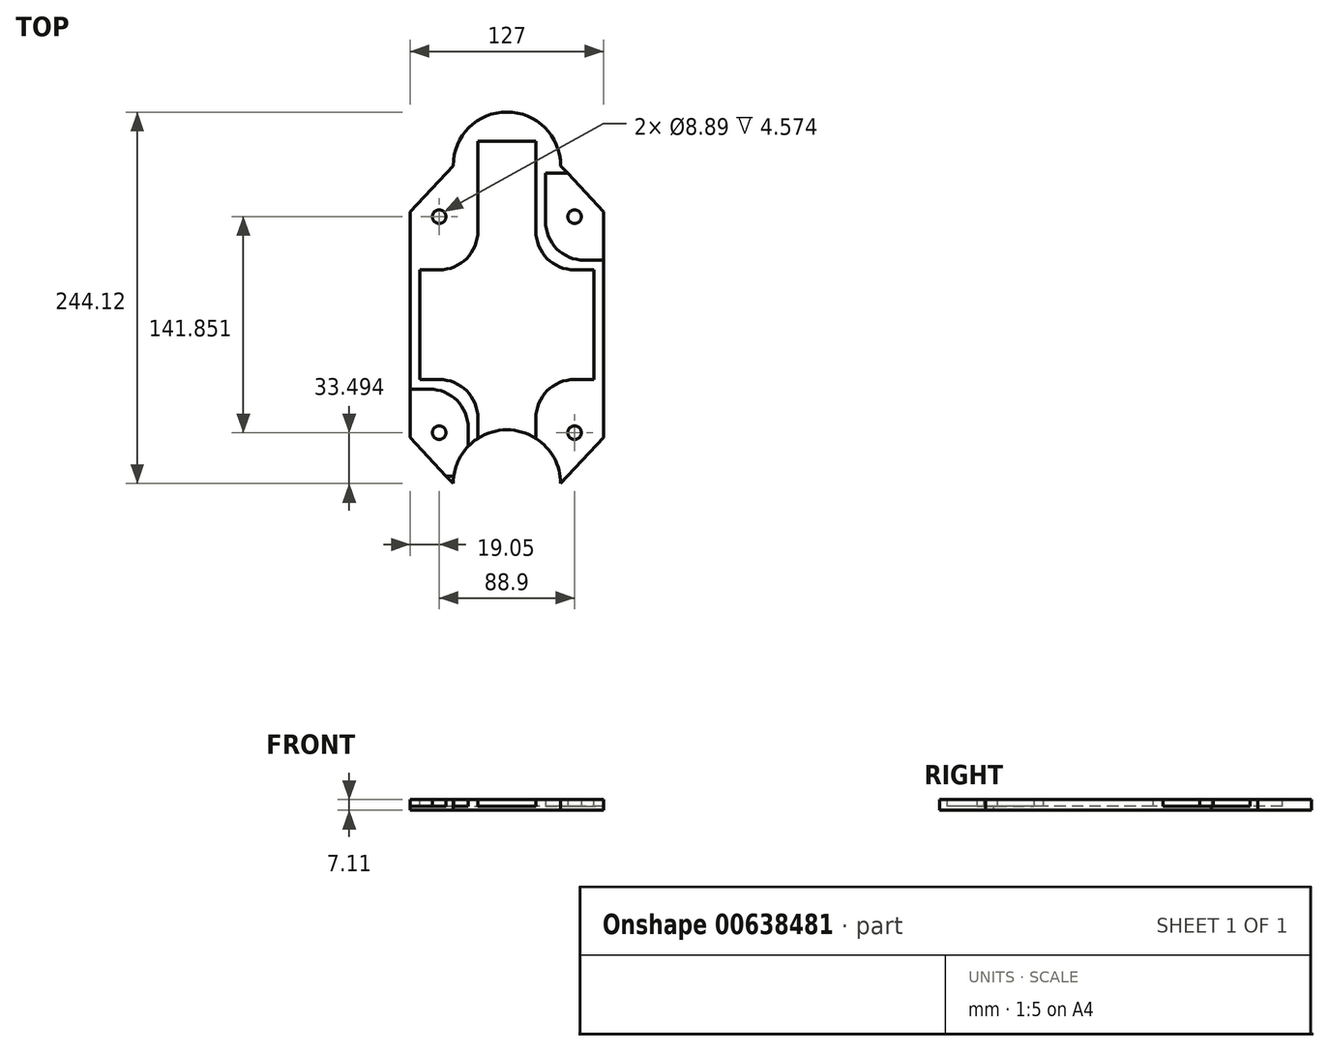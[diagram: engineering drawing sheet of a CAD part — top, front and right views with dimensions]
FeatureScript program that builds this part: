
annotation { "Feature Type Name" : "Feature", "Feature Type Description" : "" }
export const myFeature = defineFeature(function(context is Context, id is Id, definition is map)
    precondition{}
    {
        {
            var Q0;
            Q0=qCreatedBy(makeId("Top.planeOp"),FACE);
            var sketch = newSketch(context, id + "F0", { "sketchPlane" : qUnion([Q0])});
            skCircle(sketch, "E0", {"center": v(0, 104.42) * mm, "radius": 35.28 * mm});
            skLineSegment(sketch, "E1.bottom", {"start": v(63.5, 74.1) * mm, "end": v(18.06, 74.1) * mm});
            skLineSegment(sketch, "E1.left", {"start": v(63.5, 74.1) * mm, "end": v(63.5, 0) * mm});
            skLineSegment(sketch, "E1.right", {"start": v(-63.5, 74.1) * mm, "end": v(-63.5, 0) * mm});
            skPoint(sketch, "E1.middle", {"position": v(0, 0) * mm});
            skLineSegment(sketch, "E2", {"start": v(35.28, 104.42) * mm, "end": v(63.5, 74.1) * mm});
            skLineSegment(sketch, "E3", {"start": v(-35.28, 104.42) * mm, "end": v(-63.5, 74.1) * mm});
            skLineSegment(sketch, "E4", {"start": v(-63.5, 0) * mm, "end": v(63.5, 0) * mm});
            skCircle(sketch, "E5.MirrorC", {"center": v(0, -104.42) * mm, "radius": 35.28 * mm});
            skLineSegment(sketch, "E6.MirrorCS", {"start": v(63.5, -74.1) * mm, "end": v(18.06, -74.1) * mm});
            skLineSegment(sketch, "E7.MirrorCS", {"start": v(63.5, -74.1) * mm, "end": v(63.5, 0) * mm});
            skLineSegment(sketch, "E8.MirrorCS", {"start": v(-63.5, -74.1) * mm, "end": v(-63.5, 0) * mm});
            skLineSegment(sketch, "E9.MirrorCS", {"start": v(35.28, -104.42) * mm, "end": v(63.5, -74.1) * mm});
            skLineSegment(sketch, "E10.MirrorCS", {"start": v(-35.28, -104.42) * mm, "end": v(-63.5, -74.1) * mm});
            skLineSegment(sketch, "E11.trimOffspring", {"start": v(-18.06, 74.1) * mm, "end": v(-63.5, 74.1) * mm});
            skLineSegment(sketch, "E12.trimOffspring", {"start": v(-18.06, -74.1) * mm, "end": v(-63.5, -74.1) * mm});
            skSolve(sketch);
        }
        {
            var Q0;
            {var subQ0=sQuery(id+"F0.wireOp",EDGE,"E1.bottom");Q0=makeQuery(id+"F0.imprint","IMPRINT",FACE,{"disambiguationData":[TD([[makeQuery(id+"F0.imprint","IMPRINT",EDGE,{"derivedFrom":subQ0}),1.0]])]});}
            var Q1;
            Q1=makeQuery(id+"F0.imprint","IMPRINT",FACE,{"disambiguationData":[TD([[makeQuery(id+"F0.imprint","IMPRINT",EDGE,{"derivedFrom":sQuery(id+"F0.wireOp",EDGE,"E4")}),-1.0]])]});
            var Q2;
            {var subQ0=sQuery(id+"F0.wireOp",EDGE,"E5.MirrorC");var subQ1=makeQuery(id+"F0.imprint","INTERSECT",VERTEX,{"derivedFrom":[subQ0,sQuery(id+"F0.wireOp",EDGE,"E9.MirrorCS")]});Q2=makeQuery(id+"F0.imprint","IMPRINT",FACE,{"disambiguationData":[TD([[makeQuery(id+"F0.imprint","IMPRINT",EDGE,{"disambiguationData":[TD([[subQ1,-1.0]])],"derivedFrom":subQ0}),-1.0]])]});}
            var Q3;
            {var subQ0=sQuery(id+"F0.wireOp",EDGE,"E10.MirrorCS");Q3=makeQuery(id+"F0.imprint","IMPRINT",FACE,{"disambiguationData":[TD([[makeQuery(id+"F0.imprint","IMPRINT",EDGE,{"derivedFrom":subQ0}),-1.0]])]});}
            var Q4;
            {var subQ0=sQuery(id+"F0.wireOp",EDGE,"E6.MirrorCS");Q4=makeQuery(id+"F0.imprint","IMPRINT",FACE,{"disambiguationData":[TD([[makeQuery(id+"F0.imprint","IMPRINT",EDGE,{"derivedFrom":subQ0}),1.0]])]});}
            var Q5;
            {var subQ0=sQuery(id+"F0.wireOp",EDGE,"E0");var subQ1=makeQuery(id+"F0.imprint","INTERSECT",VERTEX,{"derivedFrom":[subQ0,sQuery(id+"F0.wireOp",EDGE,"E2")]});Q5=makeQuery(id+"F0.imprint","IMPRINT",FACE,{"disambiguationData":[TD([[makeQuery(id+"F0.imprint","IMPRINT",EDGE,{"disambiguationData":[TD([[subQ1,-1.0]])],"derivedFrom":subQ0}),1.0]])]});}
            var Q6;
            {var subQ0=sQuery(id+"F0.wireOp",EDGE,"E1.bottom");Q6=makeQuery(id+"F0.imprint","IMPRINT",FACE,{"disambiguationData":[TD([[makeQuery(id+"F0.imprint","IMPRINT",EDGE,{"derivedFrom":subQ0}),-1.0]])]});}
            var Q7;
            {var subQ0=sQuery(id+"F0.wireOp",EDGE,"E3");Q7=makeQuery(id+"F0.imprint","IMPRINT",FACE,{"disambiguationData":[TD([[makeQuery(id+"F0.imprint","IMPRINT",EDGE,{"derivedFrom":subQ0}),1.0]])]});}
            extrude(context, id + "F1", {"entities" : qUnion([Q0, Q1, Q2, Q3, Q4, Q5, Q6, Q7]), "depth" : 50.8 * mm, "offsetDistance" : 25.4 * mm});
        }
        {
            var Q0;
            Q0=makeQuery(id+"F1.opExtrude","SWEPT_FACE",FACE,{"disambiguationData":[OSD([sQuery(id+"F0.wireOp",EDGE,"E1.left"),sQuery(id+"F0.wireOp",EDGE,"E7.MirrorCS")])]});
            var sketch = newSketch(context, id + "F2", { "sketchPlane" : qUnion([Q0])});
            skLineSegment(sketch, "E13.0.0", {"start": v(-74.1, 0) * mm, "end": v(74.1, 0) * mm});
            skLineSegment(sketch, "E13.0.1", {"start": v(74.1, 0) * mm, "end": v(74.1, 50.8) * mm});
            skLineSegment(sketch, "E13.0.2", {"start": v(74.1, 50.8) * mm, "end": v(-74.1, 50.8) * mm});
            skLineSegment(sketch, "E13.0.3", {"start": v(-74.1, 50.8) * mm, "end": v(-74.1, 0) * mm});
            skLineSegment(sketch, "E14.0.0", {"start": v(-104.42, 0) * mm, "end": v(-74.1, 0) * mm});
            skLineSegment(sketch, "E14.0.1", {"start": v(-74.1, 0) * mm, "end": v(-74.1, 50.8) * mm});
            skLineSegment(sketch, "E14.0.2", {"start": v(-74.1, 50.8) * mm, "end": v(-104.42, 50.8) * mm});
            skLineSegment(sketch, "E14.0.3", {"start": v(-104.42, 50.8) * mm, "end": v(-104.42, 0) * mm});
            skLineSegment(sketch, "E15.bottom", {"start": v(-42.35, 43.18) * mm, "end": v(-99.5, 43.18) * mm});
            skLineSegment(sketch, "E15.top", {"start": v(-42.35, 7.62) * mm, "end": v(-99.5, 7.62) * mm});
            skLineSegment(sketch, "E15.left", {"start": v(-42.35, 43.18) * mm, "end": v(-42.35, 7.62) * mm});
            skLineSegment(sketch, "E15.right", {"start": v(-99.5, 43.18) * mm, "end": v(-99.5, 7.62) * mm});
            skLineSegment(sketch, "E16.MirrorCS", {"start": v(99.5, 43.18) * mm, "end": v(99.5, 7.62) * mm});
            skLineSegment(sketch, "E17.MirrorCS", {"start": v(42.35, 43.18) * mm, "end": v(42.35, 7.62) * mm});
            skLineSegment(sketch, "E18.MirrorCS", {"start": v(42.35, 7.62) * mm, "end": v(99.5, 7.62) * mm});
            skLineSegment(sketch, "E19.MirrorCS", {"start": v(42.35, 43.18) * mm, "end": v(99.5, 43.18) * mm});
            skSolve(sketch);
        }
        {
            var Q0;
            {var subQ5=sQuery(id+"F2.wireOp",EDGE,"E15.left");Q0=makeQuery(id+"F2.imprint","IMPRINT",FACE,{"disambiguationData":[TD([[makeQuery(id+"F2.imprint","IMPRINT",EDGE,{"derivedFrom":subQ5}),-1.0]])]});}
            var Q1;
            {var subQ5=sQuery(id+"F2.wireOp",EDGE,"E15.right");Q1=makeQuery(id+"F2.imprint","IMPRINT",FACE,{"disambiguationData":[TD([[makeQuery(id+"F2.imprint","IMPRINT",EDGE,{"derivedFrom":subQ5}),1.0]])]});}
            var Q2;
            {var subQ5=sQuery(id+"F2.wireOp",EDGE,"E16.MirrorCS");Q2=makeQuery(id+"F2.imprint","IMPRINT",FACE,{"disambiguationData":[TD([[makeQuery(id+"F2.imprint","IMPRINT",EDGE,{"derivedFrom":subQ5}),-1.0]])]});}
            var Q3;
            {var subQ5=sQuery(id+"F2.wireOp",EDGE,"E17.MirrorCS");Q3=makeQuery(id+"F2.imprint","IMPRINT",FACE,{"disambiguationData":[TD([[makeQuery(id+"F2.imprint","IMPRINT",EDGE,{"derivedFrom":subQ5}),1.0]])]});}
            extrude(context, id + "F3", {"entities" : qUnion([Q0, Q1, Q2, Q3]), "operationType" : NewBodyOperationType.REMOVE, "oppositeDirection" : true, "depth" : 38.1 * mm, "offsetDistance" : 25.4 * mm});
        }
        {
            var Q0;
            Q0=makeQuery(id+"F1.opExtrude","SWEPT_FACE",FACE,{"disambiguationData":[OSD([sQuery(id+"F0.wireOp",EDGE,"E1.right"),sQuery(id+"F0.wireOp",EDGE,"E8.MirrorCS")])]});
            var sketch = newSketch(context, id + "F4", { "sketchPlane" : qUnion([Q0])});
            skLineSegment(sketch, "E20.bottom", {"start": v(-99.5, 43.18) * mm, "end": v(-42.35, 43.18) * mm});
            skLineSegment(sketch, "E20.top", {"start": v(-99.5, 7.62) * mm, "end": v(-42.35, 7.62) * mm});
            skLineSegment(sketch, "E20.left", {"start": v(-99.5, 43.18) * mm, "end": v(-99.5, 7.62) * mm});
            skLineSegment(sketch, "E20.right", {"start": v(-42.35, 43.18) * mm, "end": v(-42.35, 7.62) * mm});
            skPoint(sketch, "E20.middle", {"position": v(-70.93, 25.4) * mm});
            skPoint(sketch, "E20.middle.positionSnap0", {"position": v(-74.1, 25.4) * mm});
            skPoint(sketch, "E20.centerSnap0", {"position": v(-74.1, 25.4) * mm});
            skPoint(sketch, "E21.MirrorP", {"position": v(74.1, 25.4) * mm});
            skLineSegment(sketch, "E22.MirrorCS", {"start": v(42.35, 43.18) * mm, "end": v(42.35, 7.62) * mm});
            skPoint(sketch, "E23.MirrorP", {"position": v(70.93, 25.4) * mm});
            skLineSegment(sketch, "E24.MirrorCS", {"start": v(99.5, 43.18) * mm, "end": v(99.5, 7.62) * mm});
            skLineSegment(sketch, "E25.MirrorCS", {"start": v(99.5, 43.18) * mm, "end": v(42.35, 43.18) * mm});
            skLineSegment(sketch, "E26.MirrorCS", {"start": v(99.5, 7.62) * mm, "end": v(42.35, 7.62) * mm});
            skSolve(sketch);
        }
        {
            var Q0;
            {var subQ0=sQuery(id+"F4.wireOp",EDGE,"E20.right");Q0=makeQuery(id+"F4.imprint","IMPRINT",FACE,{"disambiguationData":[TD([[makeQuery(id+"F4.imprint","IMPRINT",EDGE,{"derivedFrom":subQ0}),-1.0]])]});}
            var Q1;
            {var subQ0=sQuery(id+"F4.wireOp",EDGE,"E20.left");Q1=makeQuery(id+"F4.imprint","IMPRINT",FACE,{"disambiguationData":[TD([[makeQuery(id+"F4.imprint","IMPRINT",EDGE,{"derivedFrom":subQ0}),1.0]])]});}
            var Q2;
            {var subQ0=sQuery(id+"F4.wireOp",EDGE,"E22.MirrorCS");Q2=makeQuery(id+"F4.imprint","IMPRINT",FACE,{"disambiguationData":[TD([[makeQuery(id+"F4.imprint","IMPRINT",EDGE,{"derivedFrom":subQ0}),1.0]])]});}
            var Q3;
            {var subQ0=sQuery(id+"F4.wireOp",EDGE,"E24.MirrorCS");Q3=makeQuery(id+"F4.imprint","IMPRINT",FACE,{"disambiguationData":[TD([[makeQuery(id+"F4.imprint","IMPRINT",EDGE,{"derivedFrom":subQ0}),-1.0]])]});}
            extrude(context, id + "F5", {"entities" : qUnion([Q0, Q1, Q2, Q3]), "operationType" : NewBodyOperationType.REMOVE, "oppositeDirection" : true, "depth" : 38.1 * mm, "offsetDistance" : 25.4 * mm});
        }
        {
            var Q0;
            Q0=makeQuery(id+"F5.boolean.opBoolean","COPY",FACE,{"derivedFrom":makeQuery(id+"F5.opExtrude","SWEPT_FACE",FACE,{"disambiguationData":[OSD([sQuery(id+"F4.wireOp",EDGE,"E20.top")])]})});
            var sketch = newSketch(context, id + "F6", { "sketchPlane" : qUnion([Q0])});
            skLineSegment(sketch, "E27.0.0", {"start": v(-63.5, 74.1) * mm, "end": v(-63.5, 42.35) * mm});
            skLineSegment(sketch, "E27.0.1", {"start": v(-63.5, 42.35) * mm, "end": v(-25.4, 42.35) * mm});
            skLineSegment(sketch, "E27.0.2", {"start": v(-25.4, 42.35) * mm, "end": v(-25.4, 99.5) * mm});
            skLineSegment(sketch, "E27.0.3", {"start": v(-25.4, 99.5) * mm, "end": v(-39.86, 99.5) * mm});
            skLineSegment(sketch, "E27.0.4", {"start": v(-39.86, 99.5) * mm, "end": v(-63.5, 74.1) * mm});
            skLineSegment(sketch, "E28.0.0", {"start": v(-39.86, -99.5) * mm, "end": v(-25.4, -99.5) * mm});
            skLineSegment(sketch, "E28.0.1", {"start": v(-25.4, -99.5) * mm, "end": v(-25.4, -42.35) * mm});
            skLineSegment(sketch, "E28.0.2", {"start": v(-25.4, -42.35) * mm, "end": v(-63.5, -42.35) * mm});
            skLineSegment(sketch, "E28.0.3", {"start": v(-63.5, -42.35) * mm, "end": v(-63.5, -74.1) * mm});
            skLineSegment(sketch, "E28.0.4", {"start": v(-63.5, -74.1) * mm, "end": v(-39.86, -99.5) * mm});
            skLineSegment(sketch, "E29.0.0", {"start": v(63.5, 74.1) * mm, "end": v(39.86, 99.5) * mm});
            skLineSegment(sketch, "E29.0.1", {"start": v(39.86, 99.5) * mm, "end": v(25.4, 99.5) * mm});
            skLineSegment(sketch, "E29.0.2", {"start": v(25.4, 99.5) * mm, "end": v(25.4, 42.35) * mm});
            skLineSegment(sketch, "E29.0.3", {"start": v(25.4, 42.35) * mm, "end": v(63.5, 42.35) * mm});
            skLineSegment(sketch, "E29.0.4", {"start": v(63.5, 42.35) * mm, "end": v(63.5, 74.1) * mm});
            skLineSegment(sketch, "E30.0.0", {"start": v(39.86, -99.5) * mm, "end": v(63.5, -74.1) * mm});
            skLineSegment(sketch, "E30.0.1", {"start": v(63.5, -74.1) * mm, "end": v(63.5, -42.35) * mm});
            skLineSegment(sketch, "E30.0.2", {"start": v(63.5, -42.35) * mm, "end": v(25.4, -42.35) * mm});
            skLineSegment(sketch, "E30.0.3", {"start": v(25.4, -42.35) * mm, "end": v(25.4, -99.5) * mm});
            skLineSegment(sketch, "E30.0.4", {"start": v(25.4, -99.5) * mm, "end": v(39.86, -99.5) * mm});
            skCircle(sketch, "E31", {"center": v(-44.45, 70.93) * mm, "radius": 4.44 * mm});
            skPoint(sketch, "E31.centerSnap0", {"position": v(-25.4, 70.93) * mm});
            skPoint(sketch, "E31.centerSnap1", {"position": v(-44.45, 42.35) * mm});
            skCircle(sketch, "E32.MirrorC", {"center": v(44.45, 70.93) * mm, "radius": 4.44 * mm});
            skCircle(sketch, "E33.MirrorC", {"center": v(-44.45, -70.93) * mm, "radius": 4.44 * mm});
            skCircle(sketch, "E34.MirrorC", {"center": v(44.45, -70.93) * mm, "radius": 4.44 * mm});
            skSolve(sketch);
        }
        {
            var Q0;
            Q0=makeQuery(id+"F6.imprint","IMPRINT",FACE,{"disambiguationData":[TD([[makeQuery(id+"F6.imprint","IMPRINT",EDGE,{"derivedFrom":sQuery(id+"F6.wireOp",EDGE,"E31")}),1.0]])]});
            var Q1;
            Q1=makeQuery(id+"F6.imprint","IMPRINT",FACE,{"disambiguationData":[TD([[makeQuery(id+"F6.imprint","IMPRINT",EDGE,{"derivedFrom":sQuery(id+"F6.wireOp",EDGE,"E33.MirrorC")}),-1.0]])]});
            var Q2;
            Q2=makeQuery(id+"F6.imprint","IMPRINT",FACE,{"disambiguationData":[TD([[makeQuery(id+"F6.imprint","IMPRINT",EDGE,{"derivedFrom":sQuery(id+"F6.wireOp",EDGE,"E32.MirrorC")}),-1.0]])]});
            var Q3;
            Q3=makeQuery(id+"F6.imprint","IMPRINT",FACE,{"disambiguationData":[TD([[makeQuery(id+"F6.imprint","IMPRINT",EDGE,{"derivedFrom":sQuery(id+"F6.wireOp",EDGE,"E34.MirrorC")}),1.0]])]});
            extrude(context, id + "F7", {"entities" : qUnion([Q0, Q1, Q2, Q3]), "operationType" : NewBodyOperationType.REMOVE, "endBound" : BoundingType.THROUGH_ALL, "depth" : 25.4 * mm, "offsetDistance" : 25.4 * mm, "hasSecondDirection" : true, "secondDirectionOppositeDirection" : true, "secondDirectionDepth" : 5.08 * mm});
        }
        {
            var Q0;
            Q0=makeQuery(id+"F1.opExtrude","CAP_FACE",FACE,{"disambiguationData":[OSD([sQuery(id+"F0.wireOp",EDGE,"E0"),sQuery(id+"F0.wireOp",EDGE,"E1.left"),sQuery(id+"F0.wireOp",EDGE,"E1.right"),sQuery(id+"F0.wireOp",EDGE,"E2"),sQuery(id+"F0.wireOp",EDGE,"E3"),sQuery(id+"F0.wireOp",EDGE,"E5.MirrorC"),sQuery(id+"F0.wireOp",EDGE,"E7.MirrorCS"),sQuery(id+"F0.wireOp",EDGE,"E8.MirrorCS"),sQuery(id+"F0.wireOp",EDGE,"E9.MirrorCS"),sQuery(id+"F0.wireOp",EDGE,"E10.MirrorCS")])],"isStart":false});
            var sketch = newSketch(context, id + "F8", { "sketchPlane" : qUnion([Q0])});
            skLineSegment(sketch, "E35.0.0", {"start": v(-63.5, 74.1) * mm, "end": v(-63.5, 42.35) * mm});
            skLineSegment(sketch, "E35.0.1", {"start": v(-63.5, 42.35) * mm, "end": v(-25.4, 42.35) * mm});
            skLineSegment(sketch, "E35.0.2", {"start": v(-25.4, 42.35) * mm, "end": v(-25.4, 99.5) * mm});
            skLineSegment(sketch, "E35.0.3", {"start": v(-25.4, 99.5) * mm, "end": v(-39.86, 99.5) * mm});
            skLineSegment(sketch, "E35.0.4", {"start": v(-39.86, 99.5) * mm, "end": v(-63.5, 74.1) * mm});
            skLineSegment(sketch, "E36.0.0", {"start": v(-39.86, -99.5) * mm, "end": v(-25.4, -99.5) * mm});
            skLineSegment(sketch, "E36.0.1", {"start": v(-25.4, -99.5) * mm, "end": v(-25.4, -42.35) * mm});
            skLineSegment(sketch, "E36.0.2", {"start": v(-25.4, -42.35) * mm, "end": v(-63.5, -42.35) * mm});
            skLineSegment(sketch, "E36.0.3", {"start": v(-63.5, -42.35) * mm, "end": v(-63.5, -74.1) * mm});
            skLineSegment(sketch, "E36.0.4", {"start": v(-63.5, -74.1) * mm, "end": v(-39.86, -99.5) * mm});
            skLineSegment(sketch, "E37.0.0", {"start": v(39.86, -99.5) * mm, "end": v(63.5, -74.1) * mm});
            skLineSegment(sketch, "E37.0.1", {"start": v(63.5, -74.1) * mm, "end": v(63.5, -42.35) * mm});
            skLineSegment(sketch, "E37.0.2", {"start": v(63.5, -42.35) * mm, "end": v(25.4, -42.35) * mm});
            skLineSegment(sketch, "E37.0.3", {"start": v(25.4, -42.35) * mm, "end": v(25.4, -99.5) * mm});
            skLineSegment(sketch, "E37.0.4", {"start": v(25.4, -99.5) * mm, "end": v(39.86, -99.5) * mm});
            skLineSegment(sketch, "E38.0.0", {"start": v(63.5, 74.1) * mm, "end": v(39.86, 99.5) * mm});
            skLineSegment(sketch, "E38.0.1", {"start": v(39.86, 99.5) * mm, "end": v(25.4, 99.5) * mm});
            skLineSegment(sketch, "E38.0.2", {"start": v(25.4, 99.5) * mm, "end": v(25.4, 42.35) * mm});
            skLineSegment(sketch, "E38.0.3", {"start": v(25.4, 42.35) * mm, "end": v(63.5, 42.35) * mm});
            skLineSegment(sketch, "E38.0.4", {"start": v(63.5, 42.35) * mm, "end": v(63.5, 74.1) * mm});
            skLineSegment(sketch, "E39.bottom", {"start": v(-57.15, 36) * mm, "end": v(57.15, 36) * mm});
            skLineSegment(sketch, "E39.top", {"start": v(-57.15, -36) * mm, "end": v(57.15, -36) * mm});
            skLineSegment(sketch, "E39.left", {"start": v(-57.15, 36) * mm, "end": v(-57.15, -36) * mm});
            skLineSegment(sketch, "E39.right", {"start": v(57.15, 36) * mm, "end": v(57.15, -36) * mm});
            skPoint(sketch, "E39.middle", {"position": v(0, 0) * mm});
            skLineSegment(sketch, "E40.bottom", {"start": v(-19.05, 120.65) * mm, "end": v(19.05, 120.65) * mm});
            skLineSegment(sketch, "E40.top", {"start": v(-19.05, -120.65) * mm, "end": v(19.05, -120.65) * mm});
            skLineSegment(sketch, "E40.left", {"start": v(-19.05, 120.65) * mm, "end": v(-19.05, -120.65) * mm});
            skLineSegment(sketch, "E40.right", {"start": v(19.05, 120.65) * mm, "end": v(19.05, -120.65) * mm});
            skSolve(sketch);
        }
        {
            var Q0;
            {var subQ0=sQuery(id+"F8.wireOp",EDGE,"E40.left");var subQ1=sQuery(id+"F8.wireOp",EDGE,"E39.bottom");var subQ2=makeQuery(id+"F8.imprint","INTERSECT",VERTEX,{"derivedFrom":[subQ1,subQ0]});Q0=makeQuery(id+"F8.imprint","IMPRINT",FACE,{"disambiguationData":[TD([[makeQuery(id+"F8.imprint","IMPRINT",EDGE,{"disambiguationData":[TD([[subQ2,-1.0]])],"derivedFrom":subQ1}),-1.0]])]});}
            var Q1;
            {var subQ0=sQuery(id+"F8.wireOp",EDGE,"E39.right");Q1=makeQuery(id+"F8.imprint","IMPRINT",FACE,{"disambiguationData":[TD([[makeQuery(id+"F8.imprint","IMPRINT",EDGE,{"derivedFrom":subQ0}),-1.0]])]});}
            var Q2;
            {var subQ5=sQuery(id+"F8.wireOp",EDGE,"E40.top");Q2=makeQuery(id+"F8.imprint","IMPRINT",FACE,{"disambiguationData":[TD([[makeQuery(id+"F8.imprint","IMPRINT",EDGE,{"derivedFrom":subQ5}),1.0]])]});}
            var Q3;
            {var subQ5=sQuery(id+"F8.wireOp",EDGE,"E40.bottom");Q3=makeQuery(id+"F8.imprint","IMPRINT",FACE,{"disambiguationData":[TD([[makeQuery(id+"F8.imprint","IMPRINT",EDGE,{"derivedFrom":subQ5}),-1.0]])]});}
            var Q4;
            {var subQ0=sQuery(id+"F8.wireOp",EDGE,"E39.left");Q4=makeQuery(id+"F8.imprint","IMPRINT",FACE,{"disambiguationData":[TD([[makeQuery(id+"F8.imprint","IMPRINT",EDGE,{"derivedFrom":subQ0}),1.0]])]});}
            extrude(context, id + "F9", {"entities" : qUnion([Q0, Q1, Q2, Q3, Q4]), "operationType" : NewBodyOperationType.REMOVE, "oppositeDirection" : true, "depth" : 48.26 * mm, "offsetDistance" : 25.4 * mm});
        }
        {
            var Q0;
            Q0=makeQuery(id+"F5.boolean.opBoolean","COPY",EDGE,{"derivedFrom":makeQuery(id+"F5.opExtrude","CAP_EDGE",EDGE,{"disambiguationData":[OSD([sQuery(id+"F4.wireOp",EDGE,"E20.right")])],"isStart":false})});
            var Q1;
            Q1=makeQuery(id+"F5.boolean.opBoolean","COPY",EDGE,{"derivedFrom":makeQuery(id+"F5.opExtrude","CAP_EDGE",EDGE,{"disambiguationData":[OSD([sQuery(id+"F4.wireOp",EDGE,"E22.MirrorCS")])],"isStart":false})});
            var Q2;
            Q2=makeQuery(id+"F3.boolean.opBoolean","COPY",EDGE,{"derivedFrom":makeQuery(id+"F3.opExtrude","CAP_EDGE",EDGE,{"disambiguationData":[OSD([sQuery(id+"F2.wireOp",EDGE,"E15.left")])],"isStart":false})});
            var Q3;
            Q3=makeQuery(id+"F3.boolean.opBoolean","COPY",EDGE,{"derivedFrom":makeQuery(id+"F3.opExtrude","CAP_EDGE",EDGE,{"disambiguationData":[OSD([sQuery(id+"F2.wireOp",EDGE,"E17.MirrorCS")])],"isStart":false})});
            var Q4;
            Q4=makeQuery(id+"F9.boolean.opBoolean","COPY",EDGE,{"derivedFrom":makeQuery(id+"F9.opExtrude","SWEPT_EDGE",EDGE,{"disambiguationData":[OSD([sQuery(id+"F8.wireOp",EDGE,"E39.top"),sQuery(id+"F8.wireOp",EDGE,"E40.right")])]})});
            var Q5;
            Q5=makeQuery(id+"F9.boolean.opBoolean","COPY",EDGE,{"derivedFrom":makeQuery(id+"F9.opExtrude","SWEPT_EDGE",EDGE,{"disambiguationData":[OSD([sQuery(id+"F8.wireOp",EDGE,"E39.top"),sQuery(id+"F8.wireOp",EDGE,"E40.left")])]})});
            var Q6;
            Q6=makeQuery(id+"F9.boolean.opBoolean","COPY",EDGE,{"derivedFrom":makeQuery(id+"F9.opExtrude","SWEPT_EDGE",EDGE,{"disambiguationData":[OSD([sQuery(id+"F8.wireOp",EDGE,"E39.bottom"),sQuery(id+"F8.wireOp",EDGE,"E40.right")])]})});
            var Q7;
            Q7=makeQuery(id+"F9.boolean.opBoolean","COPY",EDGE,{"derivedFrom":makeQuery(id+"F9.opExtrude","SWEPT_EDGE",EDGE,{"disambiguationData":[OSD([sQuery(id+"F8.wireOp",EDGE,"E39.bottom"),sQuery(id+"F8.wireOp",EDGE,"E40.left")])]})});
            fillet(context, id + "F10", {"entities" : qUnion([Q0, Q1, Q2, Q3, Q4, Q5, Q6, Q7]), "radius" : 25.4 * mm, "tangentPropagation" : true, "allowEdgeOverflow" : false});
        }
        {
            var Q0;
            Q0=qCreatedBy(makeId("Front.planeOp"),FACE);
            var sketch = newSketch(context, id + "F11", { "sketchPlane" : qUnion([Q0])});
            skPoint(sketch, "E41.0", {"position": v(-63.5, 7.62) * mm});
            skPoint(sketch, "E42.0", {"position": v(-63.5, 50.8) * mm});
            skLineSegment(sketch, "E43.bottom", {"start": v(-63.5, 50.8) * mm, "end": v(70.08, 50.8) * mm});
            skLineSegment(sketch, "E43.top", {"start": v(-63.5, 7.11) * mm, "end": v(70.08, 7.11) * mm});
            skLineSegment(sketch, "E43.left", {"start": v(-63.5, 50.8) * mm, "end": v(-63.5, 7.11) * mm});
            skLineSegment(sketch, "E43.right", {"start": v(70.08, 50.8) * mm, "end": v(70.08, 7.11) * mm});
            skSolve(sketch);
        }
        {
            var Q0;
            Q0 = qSketchRegion(id + "F11", true);
            extrude(context, id + "F12", {"entities" : qUnion([Q0]), "operationType" : NewBodyOperationType.REMOVE, "endBound" : BoundingType.SYMMETRIC, "depth" : 352.04 * mm, "offsetDistance" : 25.4 * mm});
        }
    });
